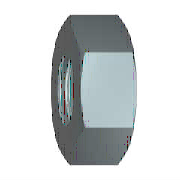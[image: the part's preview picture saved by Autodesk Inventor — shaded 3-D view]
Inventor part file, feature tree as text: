
AUTODESK INVENTOR PART (.ipt)
format: ipt  version: 2014 SP1 (Build 180222100, 222)  size: 172,032 bytes
history: native  units: mm (DEFAULTED — no unit token found)
features: sketch x3, chamfer x1, hole x1, other x1, plane x1
ambient origin geometry x7: Origin, YZ Plane, XZ Plane, X Axis, Y Axis, Z Axis, Center Point
bodies: Solid1 (feature_tree), Body (feature_tree)
feature tree (7):
  chamfer  "Chamfer1"  Angle=30.0deg  [1 undecoded]
  hole  "Thread"  [1 undecoded]
  other  "Work Axis1"
  plane  "Work Plane1"
  sketch  "Sketch1"  dims[d0=9.237604mm]
  sketch  "Sketch2"  dims[d1=5.6mm]
  sketch  "Sketch3"  dims[d2=0.0mm d3=30.0deg d4=30.0deg d5=8.0mm d6=8.0mm d7=90.0deg d25=4.134mm d26=6.0mm d27=4.0mm d28=2.0mm d29=14.3117mm d30=8.0mm d31=20.594885mm d8=0.433013mm d9=30.0deg d10=0.433013mm d11=30.0deg d13=0.0mm d14=0.0mm d39=0.0mm d40=0.433013mm d41=0.433013mm d42=0.0mm]
note: 2 required parameter values undecoded (feature->parameter linkage not recoverable at this tier; creation-order binding heuristic only, values carry confidence <= 0.55)
